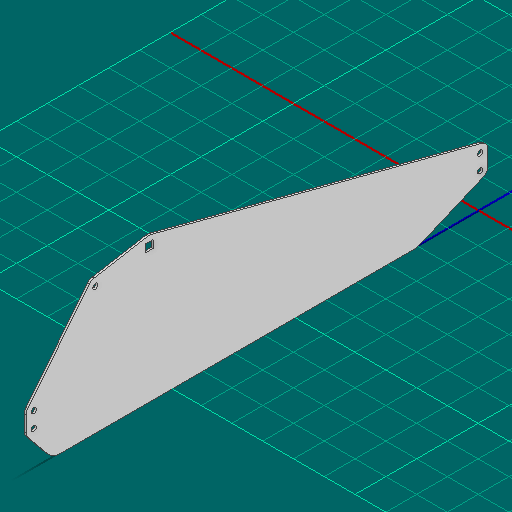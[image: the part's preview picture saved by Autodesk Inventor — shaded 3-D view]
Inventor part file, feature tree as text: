
AUTODESK INVENTOR PART (.ipt)
format: ipt  version: 2025 (Build 290162000, 162)  size: 155,648 bytes
history: native  units: in
note: dims shown in document units (in); Inventor stores cm internally (conversion verified against a paired STEP export)
features: other x6, sketch x1
ambient origin geometry x8: Origin, YZ Plane, XZ Plane, XY Plane, X Axis, Y Axis, Z Axis, Center Point
bodies: Solid1 (feature_tree)
feature tree (7):
  other  "skirt_updated.ipt"
  other  "Blocks"
  other  "maiin"
  other  "main"
  other  "Solid1::skirt_updated.ipt"
  other  "TaggingFeature1"
  sketch  "Sketch1"  dims[d0=0.3937in d1=0.5in d2=1.0in d6=0.5in d7=1.0in d10=0.625in]
